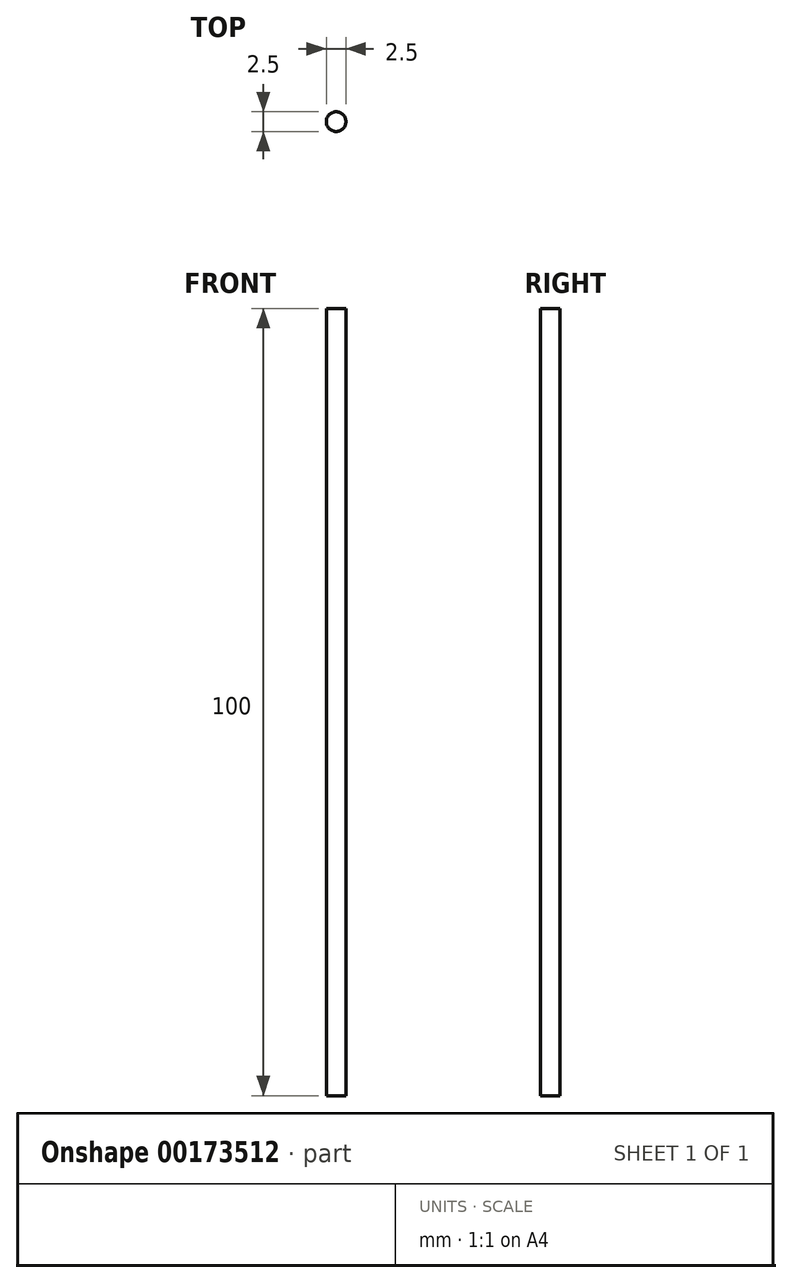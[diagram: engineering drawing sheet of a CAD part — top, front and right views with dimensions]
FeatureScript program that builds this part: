
annotation { "Feature Type Name" : "Feature", "Feature Type Description" : "" }
export const myFeature = defineFeature(function(context is Context, id is Id, definition is map)
    precondition{}
    {
        {
            var Q0;
            Q0=qCreatedBy(makeId("Top.planeOp"),FACE);
            var sketch = newSketch(context, id + "F0", { "sketchPlane" : qUnion([Q0])});
            skCircle(sketch, "E0", {"center": v(0, 0) * mm, "radius": 1.25 * mm});
            skLineSegment(sketch, "E1", {"start": v(0.63, -2.35) * mm, "end": v(-0.63, -2.35) * mm});
            skLineSegment(sketch, "E2", {"start": v(-0.83, -2.55) * mm, "end": v(-0.83, -2.77) * mm});
            skLineSegment(sketch, "E3", {"start": v(-0.98, -2.97) * mm, "end": v(-2.5, -3.31) * mm});
            skLineSegment(sketch, "E4", {"start": v(-2.9, -3.8) * mm, "end": v(-2.9, -5.9) * mm});
            skLineSegment(sketch, "E5", {"start": v(-2.7, -6.1) * mm, "end": v(-2.1, -6.1) * mm});
            skLineSegment(sketch, "E6", {"start": v(-1.6, -6.6) * mm, "end": v(-1.6, -7) * mm});
            skLineSegment(sketch, "E7", {"start": v(-4.4, -7) * mm, "end": v(-4.4, -6.67) * mm});
            skLineSegment(sketch, "E8", {"start": v(-5.25, -6.31) * mm, "end": v(-6.3, -7.35) * mm});
            skLineSegment(sketch, "E9", {"start": v(-7.35, -6.3) * mm, "end": v(-6.31, -5.25) * mm});
            skLineSegment(sketch, "E10", {"start": v(-6.67, -4.4) * mm, "end": v(-7, -4.4) * mm});
            skLineSegment(sketch, "E11", {"start": v(-7.5, -2.1) * mm, "end": v(-7.5, -3.9) * mm});
            skLineSegment(sketch, "E12", {"start": v(-7, -1.6) * mm, "end": v(-6.6, -1.6) * mm});
            skLineSegment(sketch, "E13", {"start": v(-6.1, -2.1) * mm, "end": v(-6.1, -2.7) * mm});
            skLineSegment(sketch, "E14", {"start": v(-5.9, -2.9) * mm, "end": v(-3.8, -2.9) * mm});
            skLineSegment(sketch, "E15", {"start": v(-3.31, -2.5) * mm, "end": v(-2.97, -0.98) * mm});
            skLineSegment(sketch, "E16", {"start": v(-2.77, -0.83) * mm, "end": v(-2.55, -0.83) * mm});
            skLineSegment(sketch, "E17", {"start": v(-2.35, -0.63) * mm, "end": v(-2.35, 0.63) * mm});
            skLineSegment(sketch, "E18", {"start": v(-2.55, 0.83) * mm, "end": v(-2.77, 0.83) * mm});
            skLineSegment(sketch, "E19", {"start": v(-2.97, 0.98) * mm, "end": v(-3.31, 2.5) * mm});
            skLineSegment(sketch, "E20", {"start": v(-3.8, 2.9) * mm, "end": v(-5.9, 2.9) * mm});
            skLineSegment(sketch, "E21", {"start": v(-6.1, 2.7) * mm, "end": v(-6.1, 2.1) * mm});
            skLineSegment(sketch, "E22", {"start": v(-6.6, 1.6) * mm, "end": v(-7, 1.6) * mm});
            skLineSegment(sketch, "E23", {"start": v(-7, 4.4) * mm, "end": v(-6.67, 4.4) * mm});
            skLineSegment(sketch, "E24", {"start": v(-6.31, 5.25) * mm, "end": v(-7.35, 6.3) * mm});
            skLineSegment(sketch, "E25", {"start": v(-6.3, 7.35) * mm, "end": v(-5.25, 6.31) * mm});
            skLineSegment(sketch, "E26", {"start": v(-4.4, 6.67) * mm, "end": v(-4.4, 7) * mm});
            skLineSegment(sketch, "E27", {"start": v(-1.6, 7) * mm, "end": v(-1.6, 6.6) * mm});
            skLineSegment(sketch, "E28", {"start": v(-2.1, 6.1) * mm, "end": v(-2.7, 6.1) * mm});
            skLineSegment(sketch, "E29", {"start": v(-2.9, 5.9) * mm, "end": v(-2.9, 3.8) * mm});
            skLineSegment(sketch, "E30", {"start": v(-2.5, 3.31) * mm, "end": v(-0.98, 2.97) * mm});
            skLineSegment(sketch, "E31", {"start": v(-0.83, 2.77) * mm, "end": v(-0.83, 2.55) * mm});
            skLineSegment(sketch, "E32", {"start": v(-0.63, 2.35) * mm, "end": v(0.63, 2.35) * mm});
            skLineSegment(sketch, "E33", {"start": v(0.83, 2.55) * mm, "end": v(0.83, 2.77) * mm});
            skLineSegment(sketch, "E34", {"start": v(0.98, 2.97) * mm, "end": v(2.5, 3.31) * mm});
            skLineSegment(sketch, "E35", {"start": v(2.9, 3.8) * mm, "end": v(2.9, 5.9) * mm});
            skLineSegment(sketch, "E36", {"start": v(2.7, 6.1) * mm, "end": v(2.1, 6.1) * mm});
            skLineSegment(sketch, "E37", {"start": v(1.6, 6.6) * mm, "end": v(1.6, 7) * mm});
            skLineSegment(sketch, "E38", {"start": v(4.4, 7) * mm, "end": v(4.4, 6.67) * mm});
            skLineSegment(sketch, "E39", {"start": v(5.25, 6.31) * mm, "end": v(6.3, 7.35) * mm});
            skLineSegment(sketch, "E40", {"start": v(7.25, 7.5) * mm, "end": v(6.65, 7.5) * mm});
            skLineSegment(sketch, "E41", {"start": v(7.35, 6.3) * mm, "end": v(6.31, 5.25) * mm});
            skLineSegment(sketch, "E42", {"start": v(6.67, 4.4) * mm, "end": v(7, 4.4) * mm});
            skLineSegment(sketch, "E43", {"start": v(7, 1.6) * mm, "end": v(6.6, 1.6) * mm});
            skLineSegment(sketch, "E44", {"start": v(6.1, 2.1) * mm, "end": v(6.1, 2.7) * mm});
            skLineSegment(sketch, "E45", {"start": v(5.9, 2.9) * mm, "end": v(3.8, 2.9) * mm});
            skLineSegment(sketch, "E46", {"start": v(3.31, 2.5) * mm, "end": v(2.97, 0.98) * mm});
            skLineSegment(sketch, "E47", {"start": v(2.77, 0.83) * mm, "end": v(2.55, 0.83) * mm});
            skLineSegment(sketch, "E48", {"start": v(2.35, 0.63) * mm, "end": v(2.35, -0.63) * mm});
            skLineSegment(sketch, "E49", {"start": v(2.55, -0.83) * mm, "end": v(2.77, -0.83) * mm});
            skLineSegment(sketch, "E50", {"start": v(2.97, -0.98) * mm, "end": v(3.31, -2.5) * mm});
            skLineSegment(sketch, "E51", {"start": v(3.8, -2.9) * mm, "end": v(5.9, -2.9) * mm});
            skLineSegment(sketch, "E52", {"start": v(6.1, -2.7) * mm, "end": v(6.1, -2.1) * mm});
            skLineSegment(sketch, "E53", {"start": v(6.6, -1.6) * mm, "end": v(7, -1.6) * mm});
            skLineSegment(sketch, "E54", {"start": v(7.5, -3.9) * mm, "end": v(7.5, -2.1) * mm});
            skLineSegment(sketch, "E55", {"start": v(7, -4.4) * mm, "end": v(6.67, -4.4) * mm});
            skLineSegment(sketch, "E56", {"start": v(6.31, -5.25) * mm, "end": v(7.35, -6.3) * mm});
            skLineSegment(sketch, "E57", {"start": v(6.65, -7.5) * mm, "end": v(7.25, -7.5) * mm});
            skLineSegment(sketch, "E58", {"start": v(6.3, -7.35) * mm, "end": v(5.25, -6.31) * mm});
            skLineSegment(sketch, "E59", {"start": v(4.4, -6.67) * mm, "end": v(4.4, -7) * mm});
            skLineSegment(sketch, "E60", {"start": v(1.6, -7) * mm, "end": v(1.6, -6.6) * mm});
            skLineSegment(sketch, "E61", {"start": v(2.1, -6.1) * mm, "end": v(2.7, -6.1) * mm});
            skLineSegment(sketch, "E62", {"start": v(2.9, -5.9) * mm, "end": v(2.9, -3.8) * mm});
            skLineSegment(sketch, "E63", {"start": v(2.5, -3.31) * mm, "end": v(0.98, -2.97) * mm});
            skLineSegment(sketch, "E64", {"start": v(0.83, -2.77) * mm, "end": v(0.83, -2.55) * mm});
            skLineSegment(sketch, "E65", {"start": v(-7.5, 3.9) * mm, "end": v(-7.5, 2.1) * mm});
            skLineSegment(sketch, "E66", {"start": v(-6.65, 7.5) * mm, "end": v(-7.25, 7.5) * mm});
            skLineSegment(sketch, "E67", {"start": v(-3.9, -7.5) * mm, "end": v(-2.1, -7.5) * mm});
            skLineSegment(sketch, "E68", {"start": v(7.5, 2.1) * mm, "end": v(7.5, 3.9) * mm});
            skLineSegment(sketch, "E69", {"start": v(-7.5, 7.25) * mm, "end": v(-7.5, 6.65) * mm});
            skLineSegment(sketch, "E70", {"start": v(7.5, -7.25) * mm, "end": v(7.5, -6.65) * mm});
            skLineSegment(sketch, "E71", {"start": v(7.5, 6.65) * mm, "end": v(7.5, 7.25) * mm});
            skLineSegment(sketch, "E72", {"start": v(-2.1, 7.5) * mm, "end": v(-3.9, 7.5) * mm});
            skLineSegment(sketch, "E73", {"start": v(-7.5, -6.65) * mm, "end": v(-7.5, -7.25) * mm});
            skLineSegment(sketch, "E74", {"start": v(3.9, 7.5) * mm, "end": v(2.1, 7.5) * mm});
            skLineSegment(sketch, "E75", {"start": v(2.1, -7.5) * mm, "end": v(3.9, -7.5) * mm});
            skLineSegment(sketch, "E76", {"start": v(-7.25, -7.5) * mm, "end": v(-6.65, -7.5) * mm});
            skArc(sketch, "E77", {"start": v(0.83, -2.55) * mm, "mid": v(0.77, -2.4) * mm, "end": v(0.63, -2.35) * mm});
            skArc(sketch, "E78", {"start": v(-0.63, -2.35) * mm, "mid": v(-0.77, -2.4) * mm, "end": v(-0.83, -2.55) * mm});
            skArc(sketch, "E79", {"start": v(-0.98, -2.97) * mm, "mid": v(-0.87, -2.9) * mm, "end": v(-0.83, -2.77) * mm});
            skArc(sketch, "E80", {"start": v(-2.5, -3.31) * mm, "mid": v(-2.8, -3.49) * mm, "end": v(-2.9, -3.8) * mm});
            skArc(sketch, "E81", {"start": v(-2.9, -5.9) * mm, "mid": v(-2.84, -6.04) * mm, "end": v(-2.7, -6.1) * mm});
            skArc(sketch, "E82", {"start": v(-1.6, -6.6) * mm, "mid": v(-1.75, -6.25) * mm, "end": v(-2.1, -6.1) * mm});
            skArc(sketch, "E83", {"start": v(-2.1, -7.5) * mm, "mid": v(-1.75, -7.35) * mm, "end": v(-1.6, -7) * mm});
            skArc(sketch, "E84", {"start": v(-4.4, -7) * mm, "mid": v(-4.25, -7.35) * mm, "end": v(-3.9, -7.5) * mm});
            skArc(sketch, "E85", {"start": v(-4.4, -6.67) * mm, "mid": v(-4.7, -6.2) * mm, "end": v(-5.25, -6.31) * mm});
            skArc(sketch, "E86", {"start": v(-6.65, -7.5) * mm, "mid": v(-6.46, -7.46) * mm, "end": v(-6.3, -7.35) * mm});
            skArc(sketch, "E87", {"start": v(-7.5, -7.25) * mm, "mid": v(-7.43, -7.43) * mm, "end": v(-7.25, -7.5) * mm});
            skArc(sketch, "E88", {"start": v(-7.35, -6.3) * mm, "mid": v(-7.46, -6.46) * mm, "end": v(-7.5, -6.65) * mm});
            skArc(sketch, "E89", {"start": v(-6.31, -5.25) * mm, "mid": v(-6.2, -4.7) * mm, "end": v(-6.67, -4.4) * mm});
            skArc(sketch, "E90", {"start": v(-7.5, -3.9) * mm, "mid": v(-7.35, -4.25) * mm, "end": v(-7, -4.4) * mm});
            skArc(sketch, "E91", {"start": v(-7, -1.6) * mm, "mid": v(-7.35, -1.75) * mm, "end": v(-7.5, -2.1) * mm});
            skArc(sketch, "E92", {"start": v(-6.1, -2.1) * mm, "mid": v(-6.25, -1.75) * mm, "end": v(-6.6, -1.6) * mm});
            skArc(sketch, "E93", {"start": v(-6.1, -2.7) * mm, "mid": v(-6.04, -2.84) * mm, "end": v(-5.9, -2.9) * mm});
            skArc(sketch, "E94", {"start": v(-3.8, -2.9) * mm, "mid": v(-3.49, -2.8) * mm, "end": v(-3.31, -2.5) * mm});
            skArc(sketch, "E95", {"start": v(-2.77, -0.83) * mm, "mid": v(-2.9, -0.87) * mm, "end": v(-2.97, -0.98) * mm});
            skArc(sketch, "E96", {"start": v(-2.55, -0.83) * mm, "mid": v(-2.4, -0.77) * mm, "end": v(-2.35, -0.63) * mm});
            skArc(sketch, "E97", {"start": v(-2.35, 0.63) * mm, "mid": v(-2.4, 0.77) * mm, "end": v(-2.55, 0.83) * mm});
            skArc(sketch, "E98", {"start": v(-2.97, 0.98) * mm, "mid": v(-2.9, 0.87) * mm, "end": v(-2.77, 0.83) * mm});
            skArc(sketch, "E99", {"start": v(-3.31, 2.5) * mm, "mid": v(-3.49, 2.8) * mm, "end": v(-3.8, 2.9) * mm});
            skArc(sketch, "E100", {"start": v(-5.9, 2.9) * mm, "mid": v(-6.04, 2.84) * mm, "end": v(-6.1, 2.7) * mm});
            skArc(sketch, "E101", {"start": v(-6.6, 1.6) * mm, "mid": v(-6.25, 1.75) * mm, "end": v(-6.1, 2.1) * mm});
            skArc(sketch, "E102", {"start": v(-7.5, 2.1) * mm, "mid": v(-7.35, 1.75) * mm, "end": v(-7, 1.6) * mm});
            skArc(sketch, "E103", {"start": v(-7, 4.4) * mm, "mid": v(-7.35, 4.25) * mm, "end": v(-7.5, 3.9) * mm});
            skArc(sketch, "E104", {"start": v(-6.67, 4.4) * mm, "mid": v(-6.2, 4.7) * mm, "end": v(-6.31, 5.25) * mm});
            skArc(sketch, "E105", {"start": v(-7.5, 6.65) * mm, "mid": v(-7.46, 6.46) * mm, "end": v(-7.35, 6.3) * mm});
            skArc(sketch, "E106", {"start": v(-7.25, 7.5) * mm, "mid": v(-7.43, 7.43) * mm, "end": v(-7.5, 7.25) * mm});
            skArc(sketch, "E107", {"start": v(-6.3, 7.35) * mm, "mid": v(-6.46, 7.46) * mm, "end": v(-6.65, 7.5) * mm});
            skArc(sketch, "E108", {"start": v(-5.25, 6.31) * mm, "mid": v(-4.7, 6.2) * mm, "end": v(-4.4, 6.67) * mm});
            skArc(sketch, "E109", {"start": v(-3.9, 7.5) * mm, "mid": v(-4.25, 7.35) * mm, "end": v(-4.4, 7) * mm});
            skArc(sketch, "E110", {"start": v(-1.6, 7) * mm, "mid": v(-1.75, 7.35) * mm, "end": v(-2.1, 7.5) * mm});
            skArc(sketch, "E111", {"start": v(-2.1, 6.1) * mm, "mid": v(-1.75, 6.25) * mm, "end": v(-1.6, 6.6) * mm});
            skArc(sketch, "E112", {"start": v(-2.7, 6.1) * mm, "mid": v(-2.84, 6.04) * mm, "end": v(-2.9, 5.9) * mm});
            skArc(sketch, "E113", {"start": v(-2.9, 3.8) * mm, "mid": v(-2.8, 3.49) * mm, "end": v(-2.5, 3.31) * mm});
            skArc(sketch, "E114", {"start": v(-0.83, 2.77) * mm, "mid": v(-0.87, 2.9) * mm, "end": v(-0.98, 2.97) * mm});
            skArc(sketch, "E115", {"start": v(-0.83, 2.55) * mm, "mid": v(-0.77, 2.4) * mm, "end": v(-0.63, 2.35) * mm});
            skArc(sketch, "E116", {"start": v(0.63, 2.35) * mm, "mid": v(0.77, 2.4) * mm, "end": v(0.83, 2.55) * mm});
            skArc(sketch, "E117", {"start": v(0.98, 2.97) * mm, "mid": v(0.87, 2.9) * mm, "end": v(0.83, 2.77) * mm});
            skArc(sketch, "E118", {"start": v(2.5, 3.31) * mm, "mid": v(2.8, 3.49) * mm, "end": v(2.9, 3.8) * mm});
            skArc(sketch, "E119", {"start": v(2.9, 5.9) * mm, "mid": v(2.84, 6.04) * mm, "end": v(2.7, 6.1) * mm});
            skArc(sketch, "E120", {"start": v(1.6, 6.6) * mm, "mid": v(1.75, 6.25) * mm, "end": v(2.1, 6.1) * mm});
            skArc(sketch, "E121", {"start": v(2.1, 7.5) * mm, "mid": v(1.75, 7.35) * mm, "end": v(1.6, 7) * mm});
            skArc(sketch, "E122", {"start": v(4.4, 7) * mm, "mid": v(4.25, 7.35) * mm, "end": v(3.9, 7.5) * mm});
            skArc(sketch, "E123", {"start": v(4.4, 6.67) * mm, "mid": v(4.7, 6.2) * mm, "end": v(5.25, 6.31) * mm});
            skArc(sketch, "E124", {"start": v(6.65, 7.5) * mm, "mid": v(6.46, 7.46) * mm, "end": v(6.3, 7.35) * mm});
            skArc(sketch, "E125", {"start": v(7.5, 7.25) * mm, "mid": v(7.43, 7.43) * mm, "end": v(7.25, 7.5) * mm});
            skArc(sketch, "E126", {"start": v(7.35, 6.3) * mm, "mid": v(7.46, 6.46) * mm, "end": v(7.5, 6.65) * mm});
            skArc(sketch, "E127", {"start": v(6.31, 5.25) * mm, "mid": v(6.2, 4.7) * mm, "end": v(6.67, 4.4) * mm});
            skArc(sketch, "E128", {"start": v(7.5, 3.9) * mm, "mid": v(7.35, 4.25) * mm, "end": v(7, 4.4) * mm});
            skArc(sketch, "E129", {"start": v(7, 1.6) * mm, "mid": v(7.35, 1.75) * mm, "end": v(7.5, 2.1) * mm});
            skArc(sketch, "E130", {"start": v(6.1, 2.1) * mm, "mid": v(6.25, 1.75) * mm, "end": v(6.6, 1.6) * mm});
            skArc(sketch, "E131", {"start": v(6.1, 2.7) * mm, "mid": v(6.04, 2.84) * mm, "end": v(5.9, 2.9) * mm});
            skArc(sketch, "E132", {"start": v(3.8, 2.9) * mm, "mid": v(3.49, 2.8) * mm, "end": v(3.31, 2.5) * mm});
            skArc(sketch, "E133", {"start": v(2.77, 0.83) * mm, "mid": v(2.9, 0.87) * mm, "end": v(2.97, 0.98) * mm});
            skArc(sketch, "E134", {"start": v(2.55, 0.83) * mm, "mid": v(2.4, 0.77) * mm, "end": v(2.35, 0.63) * mm});
            skArc(sketch, "E135", {"start": v(2.35, -0.63) * mm, "mid": v(2.4, -0.77) * mm, "end": v(2.55, -0.83) * mm});
            skArc(sketch, "E136", {"start": v(2.97, -0.98) * mm, "mid": v(2.9, -0.87) * mm, "end": v(2.77, -0.83) * mm});
            skArc(sketch, "E137", {"start": v(3.31, -2.5) * mm, "mid": v(3.49, -2.8) * mm, "end": v(3.8, -2.9) * mm});
            skArc(sketch, "E138", {"start": v(5.9, -2.9) * mm, "mid": v(6.04, -2.84) * mm, "end": v(6.1, -2.7) * mm});
            skArc(sketch, "E139", {"start": v(6.6, -1.6) * mm, "mid": v(6.25, -1.75) * mm, "end": v(6.1, -2.1) * mm});
            skArc(sketch, "E140", {"start": v(7.5, -2.1) * mm, "mid": v(7.35, -1.75) * mm, "end": v(7, -1.6) * mm});
            skArc(sketch, "E141", {"start": v(7, -4.4) * mm, "mid": v(7.35, -4.25) * mm, "end": v(7.5, -3.9) * mm});
            skArc(sketch, "E142", {"start": v(6.67, -4.4) * mm, "mid": v(6.2, -4.7) * mm, "end": v(6.31, -5.25) * mm});
            skArc(sketch, "E143", {"start": v(7.5, -6.65) * mm, "mid": v(7.46, -6.46) * mm, "end": v(7.35, -6.3) * mm});
            skArc(sketch, "E144", {"start": v(7.25, -7.5) * mm, "mid": v(7.43, -7.43) * mm, "end": v(7.5, -7.25) * mm});
            skArc(sketch, "E145", {"start": v(6.3, -7.35) * mm, "mid": v(6.46, -7.46) * mm, "end": v(6.65, -7.5) * mm});
            skArc(sketch, "E146", {"start": v(5.25, -6.31) * mm, "mid": v(4.7, -6.2) * mm, "end": v(4.4, -6.67) * mm});
            skArc(sketch, "E147", {"start": v(3.9, -7.5) * mm, "mid": v(4.25, -7.35) * mm, "end": v(4.4, -7) * mm});
            skArc(sketch, "E148", {"start": v(1.6, -7) * mm, "mid": v(1.75, -7.35) * mm, "end": v(2.1, -7.5) * mm});
            skArc(sketch, "E149", {"start": v(2.1, -6.1) * mm, "mid": v(1.75, -6.25) * mm, "end": v(1.6, -6.6) * mm});
            skArc(sketch, "E150", {"start": v(2.7, -6.1) * mm, "mid": v(2.84, -6.04) * mm, "end": v(2.9, -5.9) * mm});
            skArc(sketch, "E151", {"start": v(2.9, -3.8) * mm, "mid": v(2.8, -3.49) * mm, "end": v(2.5, -3.31) * mm});
            skArc(sketch, "E152", {"start": v(0.83, -2.77) * mm, "mid": v(0.87, -2.9) * mm, "end": v(0.98, -2.97) * mm});
            skSolve(sketch);
        }
        {
            var Q0;
            Q0=makeQuery(id+"F0.imprint","IMPRINT",FACE,{"disambiguationData":[TD([[makeQuery(id+"F0.imprint","IMPRINT",EDGE,{"derivedFrom":sQuery(id+"F0.wireOp",EDGE,"E0")}),1.0]])]});
            var Q1;
            Q1=sQuery(id+"F0.wireOp",EDGE,"E58");
            var Q2;
            Q2=sQuery(id+"F0.wireOp",EDGE,"E122");
            var Q3;
            Q3=sQuery(id+"F0.wireOp",EDGE,"E90");
            var Q4;
            Q4=sQuery(id+"F0.wireOp",EDGE,"E74");
            var Q5;
            Q5=sQuery(id+"F0.wireOp",EDGE,"E19");
            var Q6;
            Q6=sQuery(id+"F0.wireOp",EDGE,"E83");
            var Q7;
            Q7=sQuery(id+"F0.wireOp",EDGE,"E67");
            var Q8;
            Q8=sQuery(id+"F0.wireOp",EDGE,"E51");
            var Q9;
            Q9=sQuery(id+"F0.wireOp",EDGE,"E35");
            var Q10;
            Q10=sQuery(id+"F0.wireOp",EDGE,"E147");
            var Q11;
            Q11=sQuery(id+"F0.wireOp",EDGE,"E99");
            var Q12;
            Q12=sQuery(id+"F0.wireOp",EDGE,"E123");
            var Q13;
            Q13=sQuery(id+"F0.wireOp",EDGE,"E91");
            var Q14;
            Q14=sQuery(id+"F0.wireOp",EDGE,"E75");
            var Q15;
            Q15=sQuery(id+"F0.wireOp",EDGE,"E139");
            var Q16;
            Q16=sQuery(id+"F0.wireOp",EDGE,"E20");
            var Q17;
            Q17=sQuery(id+"F0.wireOp",EDGE,"E84");
            var Q18;
            Q18=sQuery(id+"F0.wireOp",EDGE,"E68");
            var Q19;
            Q19=sQuery(id+"F0.wireOp",EDGE,"E45");
            var Q20;
            Q20=sQuery(id+"F0.wireOp",EDGE,"E29");
            var Q21;
            Q21=sQuery(id+"F0.wireOp",EDGE,"E148");
            var Q22;
            Q22=sQuery(id+"F0.wireOp",EDGE,"E141");
            var Q23;
            Q23=sQuery(id+"F0.wireOp",EDGE,"E109");
            var Q24;
            Q24=sQuery(id+"F0.wireOp",EDGE,"E132");
            var Q25;
            Q25=sQuery(id+"F0.wireOp",EDGE,"E108");
            var Q26;
            Q26=sQuery(id+"F0.wireOp",EDGE,"E92");
            var Q27;
            Q27=sQuery(id+"F0.wireOp",EDGE,"E140");
            var Q28;
            Q28=sQuery(id+"F0.wireOp",EDGE,"E85");
            var Q29;
            Q29=sQuery(id+"F0.wireOp",EDGE,"E62");
            var Q30;
            Q30=sQuery(id+"F0.wireOp",EDGE,"E46");
            var Q31;
            Q31=sQuery(id+"F0.wireOp",EDGE,"E30");
            var Q32;
            Q32=sQuery(id+"F0.wireOp",EDGE,"E149");
            var Q33;
            Q33=sQuery(id+"F0.wireOp",EDGE,"E142");
            var Q34;
            Q34=sQuery(id+"F0.wireOp",EDGE,"E110");
            var Q35;
            Q35=sQuery(id+"F0.wireOp",EDGE,"E94");
            var Q36;
            Q36=sQuery(id+"F0.wireOp",EDGE,"E101");
            var Q37;
            Q37=sQuery(id+"F0.wireOp",EDGE,"E63");
            var Q38;
            Q38=sQuery(id+"F0.wireOp",EDGE,"E54");
            var Q39;
            Q39=sQuery(id+"F0.wireOp",EDGE,"E127");
            var Q40;
            Q40=sQuery(id+"F0.wireOp",EDGE,"E118");
            var Q41;
            Q41=sQuery(id+"F0.wireOp",EDGE,"E111");
            var Q42;
            Q42=sQuery(id+"F0.wireOp",EDGE,"E14");
            var Q43;
            Q43=sQuery(id+"F0.wireOp",EDGE,"E15");
            var Q44;
            Q44=sQuery(id+"F0.wireOp",EDGE,"E1");
            var Q45;
            Q45=sQuery(id+"F0.wireOp",EDGE,"E3");
            var Q46;
            Q46=sQuery(id+"F0.wireOp",EDGE,"E4");
            var Q47;
            Q47=sQuery(id+"F0.wireOp",EDGE,"E8");
            var Q48;
            Q48=sQuery(id+"F0.wireOp",EDGE,"E9");
            var Q49;
            Q49=sQuery(id+"F0.wireOp",EDGE,"E11");
            var Q50;
            Q50=sQuery(id+"F0.wireOp",EDGE,"E102");
            var Q51;
            Q51=sQuery(id+"F0.wireOp",EDGE,"E128");
            var Q52;
            Q52=sQuery(id+"F0.wireOp",EDGE,"E39");
            var Q53;
            Q53=sQuery(id+"F0.wireOp",EDGE,"E103");
            var Q54;
            Q54=sQuery(id+"F0.wireOp",EDGE,"E80");
            var Q55;
            Q55=sQuery(id+"F0.wireOp",EDGE,"E48");
            var Q56;
            Q56=sQuery(id+"F0.wireOp",EDGE,"E32");
            var Q57;
            Q57=sQuery(id+"F0.wireOp",EDGE,"E151");
            var Q58;
            Q58=sQuery(id+"F0.wireOp",EDGE,"E56");
            var Q59;
            Q59=sQuery(id+"F0.wireOp",EDGE,"E24");
            var Q60;
            Q60=sQuery(id+"F0.wireOp",EDGE,"E120");
            var Q61;
            Q61=sQuery(id+"F0.wireOp",EDGE,"E104");
            var Q62;
            Q62=sQuery(id+"F0.wireOp",EDGE,"E72");
            var Q63;
            Q63=sQuery(id+"F0.wireOp",EDGE,"E17");
            var Q64;
            Q64=sQuery(id+"F0.wireOp",EDGE,"E65");
            var Q65;
            Q65=sQuery(id+"F0.wireOp",EDGE,"E129");
            var Q66;
            Q66=sQuery(id+"F0.wireOp",EDGE,"E41");
            var Q67;
            Q67=sQuery(id+"F0.wireOp",EDGE,"E25");
            var Q68;
            Q68=sQuery(id+"F0.wireOp",EDGE,"E121");
            var Q69;
            Q69=sQuery(id+"F0.wireOp",EDGE,"E89");
            var Q70;
            Q70=sQuery(id+"F0.wireOp",EDGE,"E82");
            var Q71;
            Q71=sQuery(id+"F0.wireOp",EDGE,"E50");
            var Q72;
            Q72=sQuery(id+"F0.wireOp",EDGE,"E34");
            var Q73;
            Q73=sQuery(id+"F0.wireOp",EDGE,"E146");
            var Q74;
            Q74=sQuery(id+"F0.wireOp",EDGE,"E130");
            var Q75;
            Q75=sQuery(id+"F0.wireOp",EDGE,"E42");
            var Q76;
            Q76=sQuery(id+"F0.wireOp",EDGE,"E26");
            var Q77;
            Q77=sQuery(id+"F0.wireOp",EDGE,"E106");
            var Q78;
            Q78=sQuery(id+"F0.wireOp",EDGE,"E138");
            var Q79;
            Q79=sQuery(id+"F0.wireOp",EDGE,"E131");
            var Q80;
            Q80=sQuery(id+"F0.wireOp",EDGE,"E115");
            var Q81;
            Q81=sQuery(id+"F0.wireOp",EDGE,"E59");
            var Q82;
            Q82=sQuery(id+"F0.wireOp",EDGE,"E43");
            var Q83;
            Q83=sQuery(id+"F0.wireOp",EDGE,"E27");
            var Q84;
            Q84=sQuery(id+"F0.wireOp",EDGE,"E107");
            var Q85;
            Q85=sQuery(id+"F0.wireOp",EDGE,"E77");
            var Q86;
            Q86=sQuery(id+"F0.wireOp",EDGE,"E61");
            var Q87;
            Q87=sQuery(id+"F0.wireOp",EDGE,"E52");
            var Q88;
            Q88=sQuery(id+"F0.wireOp",EDGE,"E36");
            var Q89;
            Q89=sQuery(id+"F0.wireOp",EDGE,"E125");
            var Q90;
            Q90=sQuery(id+"F0.wireOp",EDGE,"E93");
            var Q91;
            Q91=sQuery(id+"F0.wireOp",EDGE,"E116");
            var Q92;
            Q92=sQuery(id+"F0.wireOp",EDGE,"E100");
            var Q93;
            Q93=sQuery(id+"F0.wireOp",EDGE,"E60");
            var Q94;
            Q94=sQuery(id+"F0.wireOp",EDGE,"E44");
            var Q95;
            Q95=sQuery(id+"F0.wireOp",EDGE,"E28");
            var Q96;
            Q96=sQuery(id+"F0.wireOp",EDGE,"E124");
            var Q97;
            Q97=sQuery(id+"F0.wireOp",EDGE,"E76");
            var Q98;
            Q98=sQuery(id+"F0.wireOp",EDGE,"E21");
            var Q99;
            Q99=sQuery(id+"F0.wireOp",EDGE,"E78");
            var Q100;
            Q100=sQuery(id+"F0.wireOp",EDGE,"E69");
            var Q101;
            Q101=sQuery(id+"F0.wireOp",EDGE,"E53");
            var Q102;
            Q102=sQuery(id+"F0.wireOp",EDGE,"E37");
            var Q103;
            Q103=sQuery(id+"F0.wireOp",EDGE,"E133");
            var Q104;
            Q104=sQuery(id+"F0.wireOp",EDGE,"E126");
            var Q105;
            Q105=sQuery(id+"F0.wireOp",EDGE,"E117");
            var Q106;
            Q106=sQuery(id+"F0.wireOp",EDGE,"E22");
            var Q107;
            Q107=sQuery(id+"F0.wireOp",EDGE,"E79");
            var Q108;
            Q108=sQuery(id+"F0.wireOp",EDGE,"E86");
            var Q109;
            Q109=sQuery(id+"F0.wireOp",EDGE,"E70");
            var Q110;
            Q110=sQuery(id+"F0.wireOp",EDGE,"E47");
            var Q111;
            Q111=sQuery(id+"F0.wireOp",EDGE,"E38");
            var Q112;
            Q112=sQuery(id+"F0.wireOp",EDGE,"E31");
            var Q113;
            Q113=sQuery(id+"F0.wireOp",EDGE,"E150");
            var Q114;
            Q114=sQuery(id+"F0.wireOp",EDGE,"E143");
            var Q115;
            Q115=sQuery(id+"F0.wireOp",EDGE,"E134");
            var Q116;
            Q116=sQuery(id+"F0.wireOp",EDGE,"E95");
            var Q117;
            Q117=sQuery(id+"F0.wireOp",EDGE,"E13");
            var Q118;
            Q118=sQuery(id+"F0.wireOp",EDGE,"E2");
            var Q119;
            Q119=sQuery(id+"F0.wireOp",EDGE,"E5");
            var Q120;
            Q120=sQuery(id+"F0.wireOp",EDGE,"E6");
            var Q121;
            Q121=sQuery(id+"F0.wireOp",EDGE,"E7");
            var Q122;
            Q122=sQuery(id+"F0.wireOp",EDGE,"E114");
            var Q123;
            Q123=sQuery(id+"F0.wireOp",EDGE,"E10");
            var Q124;
            Q124=sQuery(id+"F0.wireOp",EDGE,"E12");
            var Q125;
            Q125=sQuery(id+"F0.wireOp",EDGE,"E144");
            var Q126;
            Q126=sQuery(id+"F0.wireOp",EDGE,"E55");
            var Q127;
            Q127=sQuery(id+"F0.wireOp",EDGE,"E23");
            var Q128;
            Q128=sQuery(id+"F0.wireOp",EDGE,"E119");
            var Q129;
            Q129=sQuery(id+"F0.wireOp",EDGE,"E87");
            var Q130;
            Q130=sQuery(id+"F0.wireOp",EDGE,"E112");
            var Q131;
            Q131=sQuery(id+"F0.wireOp",EDGE,"E96");
            var Q132;
            Q132=sQuery(id+"F0.wireOp",EDGE,"E71");
            var Q133;
            Q133=sQuery(id+"F0.wireOp",EDGE,"E16");
            var Q134;
            Q134=sQuery(id+"F0.wireOp",EDGE,"E64");
            var Q135;
            Q135=sQuery(id+"F0.wireOp",EDGE,"E135");
            var Q136;
            Q136=sQuery(id+"F0.wireOp",EDGE,"E40");
            var Q137;
            Q137=sQuery(id+"F0.wireOp",EDGE,"E88");
            var Q138;
            Q138=sQuery(id+"F0.wireOp",EDGE,"E152");
            var Q139;
            Q139=sQuery(id+"F0.wireOp",EDGE,"E136");
            var Q140;
            Q140=sQuery(id+"F0.wireOp",EDGE,"E81");
            var Q141;
            Q141=sQuery(id+"F0.wireOp",EDGE,"E49");
            var Q142;
            Q142=sQuery(id+"F0.wireOp",EDGE,"E33");
            var Q143;
            Q143=sQuery(id+"F0.wireOp",EDGE,"E145");
            var Q144;
            Q144=sQuery(id+"F0.wireOp",EDGE,"E113");
            var Q145;
            Q145=sQuery(id+"F0.wireOp",EDGE,"E97");
            var Q146;
            Q146=sQuery(id+"F0.wireOp",EDGE,"E57");
            var Q147;
            Q147=sQuery(id+"F0.wireOp",EDGE,"E105");
            var Q148;
            Q148=sQuery(id+"F0.wireOp",EDGE,"E73");
            var Q149;
            Q149=sQuery(id+"F0.wireOp",EDGE,"E137");
            var Q150;
            Q150=sQuery(id+"F0.wireOp",EDGE,"E18");
            var Q151;
            Q151=sQuery(id+"F0.wireOp",EDGE,"E66");
            var Q152;
            Q152=sQuery(id+"F0.wireOp",EDGE,"E98");
            extrude(context, id + "F1", {"entities" : qUnion([Q0]), "surfaceEntities" : qUnion([Q1, Q2, Q3, Q4, Q5, Q6, Q7, Q8, Q9, Q10, Q11, Q12, Q13, Q14, Q15, Q16, Q17, Q18, Q19, Q20, Q21, Q22, Q23, Q24, Q25, Q26, Q27, Q28, Q29, Q30, Q31, Q32, Q33, Q34, Q35, Q36, Q37, Q38, Q39, Q40, Q41, Q42, Q43, Q44, Q45, Q46, Q47, Q48, Q49, Q50, Q51, Q52, Q53, Q54, Q55, Q56, Q57, Q58, Q59, Q60, Q61, Q62, Q63, Q64, Q65, Q66, Q67, Q68, Q69, Q70, Q71, Q72, Q73, Q74, Q75, Q76, Q77, Q78, Q79, Q80, Q81, Q82, Q83, Q84, Q85, Q86, Q87, Q88, Q89, Q90, Q91, Q92, Q93, Q94, Q95, Q96, Q97, Q98, Q99, Q100, Q101, Q102, Q103, Q104, Q105, Q106, Q107, Q108, Q109, Q110, Q111, Q112, Q113, Q114, Q115, Q116, Q117, Q118, Q119, Q120, Q121, Q122, Q123, Q124, Q125, Q126, Q127, Q128, Q129, Q130, Q131, Q132, Q133, Q134, Q135, Q136, Q137, Q138, Q139, Q140, Q141, Q142, Q143, Q144, Q145, Q146, Q147, Q148, Q149, Q150, Q151, Q152]), "depth" : 100 * mm});
        }
    });
